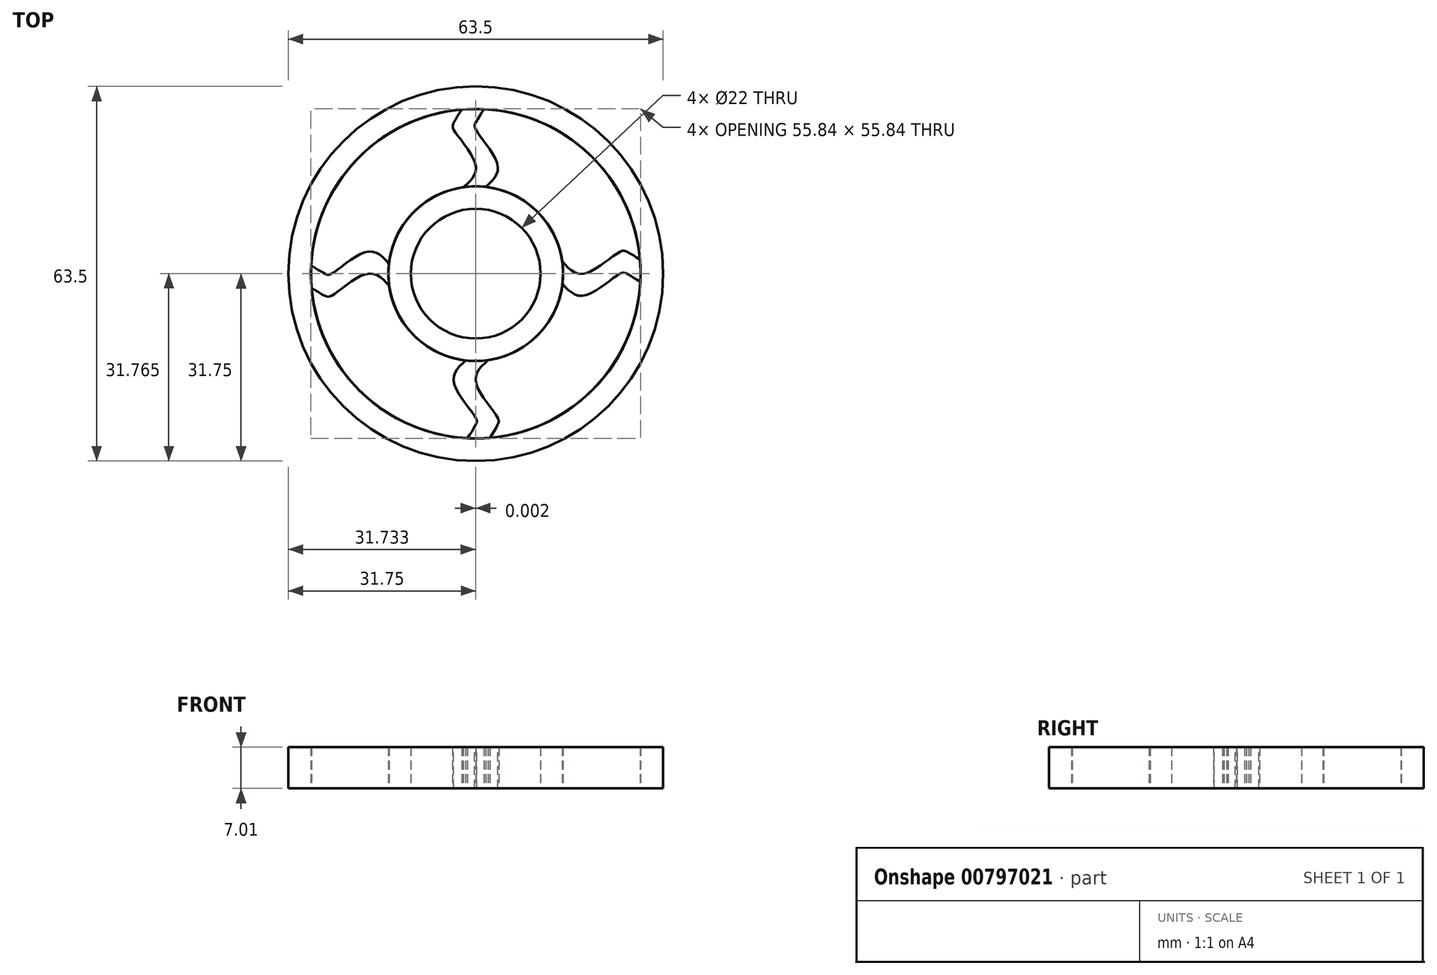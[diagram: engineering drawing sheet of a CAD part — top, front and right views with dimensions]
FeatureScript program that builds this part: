
annotation { "Feature Type Name" : "Feature", "Feature Type Description" : "" }
export const myFeature = defineFeature(function(context is Context, id is Id, definition is map)
    precondition{}
    {
        {
            var Q0;
            Q0=qCreatedBy(makeId("Top.planeOp"),FACE);
            var sketch = newSketch(context, id + "F0", { "sketchPlane" : qUnion([Q0])});
            skCircle(sketch, "E0", {"center": v(0, 0) * mm, "radius": 11 * mm});
            skCircle(sketch, "E1", {"center": v(0, 0) * mm, "radius": 31.75 * mm});
            skCircle(sketch, "E2", {"center": v(0, 0) * mm, "radius": 14.8 * mm});
            skCircle(sketch, "E3", {"center": v(0, 0) * mm, "radius": 27.94 * mm});
            skSolve(sketch);
        }
        {
            var Q0;
            Q0=makeQuery(id+"F0.imprint","IMPRINT",FACE,{"disambiguationData":[TD([[makeQuery(id+"F0.imprint","IMPRINT",EDGE,{"derivedFrom":sQuery(id+"F0.wireOp",EDGE,"E0")}),-1.0]])]});
            var Q1;
            Q1=makeQuery(id+"F0.imprint","IMPRINT",FACE,{"disambiguationData":[TD([[makeQuery(id+"F0.imprint","IMPRINT",EDGE,{"derivedFrom":sQuery(id+"F0.wireOp",EDGE,"E1")}),1.0]])]});
            extrude(context, id + "F1", {"entities" : qUnion([Q0, Q1]), "depth" : 7 * mm, "offsetDistance" : 25.4 * mm});
        }
        {
            var Q0;
            Q0=qCreatedBy(makeId("Top.planeOp"),FACE);
            var sketch = newSketch(context, id + "F2", { "sketchPlane" : qUnion([Q0])});
            skFitSpline(sketch, "E4", {"points": [v(1.35, 14.42) * mm, v(3.74, 18.24) * mm, v(0, 24.44) * mm, v(0, 25.6) * mm, v(2.24, 29.2) * mm], "startDerivative": vector(14.7, 12.34) * mm, "endDerivative": vector(10.65, 16.32) * mm});
            skFitSpline(sketch, "E5", {"points": [v(-2.38, 14.42) * mm, v(0, 18.24) * mm, v(-3.73, 24.44) * mm, v(-3.73, 25.6) * mm, v(-1.5, 29.2) * mm], "startDerivative": vector(14.7, 12.34) * mm, "endDerivative": vector(10.65, 16.32) * mm});
            skLineSegment(sketch, "E6", {"start": v(2.24, 29.2) * mm, "end": v(-1.5, 29.2) * mm});
            skLineSegment(sketch, "E7", {"start": v(1.35, 14.42) * mm, "end": v(-2.38, 14.42) * mm});
            skSolve(sketch);
        }
        {
            var Q0;
            Q0 = qSketchRegion(id + "F2", true);
            var Q1;
            Q1=makeQuery(id+"F1.opExtrude","CAP_FACE",FACE,{"disambiguationData":[OSD([sQuery(id+"F0.wireOp",EDGE,"E0"),sQuery(id+"F0.wireOp",EDGE,"E2")])],"isStart":false});
            extrude(context, id + "F3", {"entities" : qUnion([Q0]), "operationType" : NewBodyOperationType.ADD, "endBound" : BoundingType.UP_TO_SURFACE, "depth" : 25.4 * mm, "endBoundEntityFace" : qUnion([Q1]), "offsetDistance" : 25.4 * mm});
        }
        {
            var Q0;
            Q0=makeQuery(id+"F3.opExtrude","SWEPT_BODY",BODY,{"disambiguationData":[OSD([sQuery(id+"F2.wireOp",EDGE,"E4"),sQuery(id+"F2.wireOp",EDGE,"E5"),sQuery(id+"F2.wireOp",EDGE,"E6"),sQuery(id+"F2.wireOp",EDGE,"E7")])]});
            var Q1;
            Q1=makeQuery(id+"F1.opExtrude","SWEPT_BODY",BODY,{"disambiguationData":[OSD([sQuery(id+"F0.wireOp",EDGE,"E0"),sQuery(id+"F0.wireOp",EDGE,"E2")])]});
            var Q2;
            Q2=makeQuery(id+"F1.opExtrude","SWEPT_FACE",FACE,{"disambiguationData":[OSD([sQuery(id+"F0.wireOp",EDGE,"E2")])]});
            circularPattern(context, id + "F4", {"entities" : qUnion([Q0, Q1]), "axis" : qUnion([Q2]), "angle" : 360 * degree, "instanceCount" : 4, "equalSpace" : true});
        }
    });
